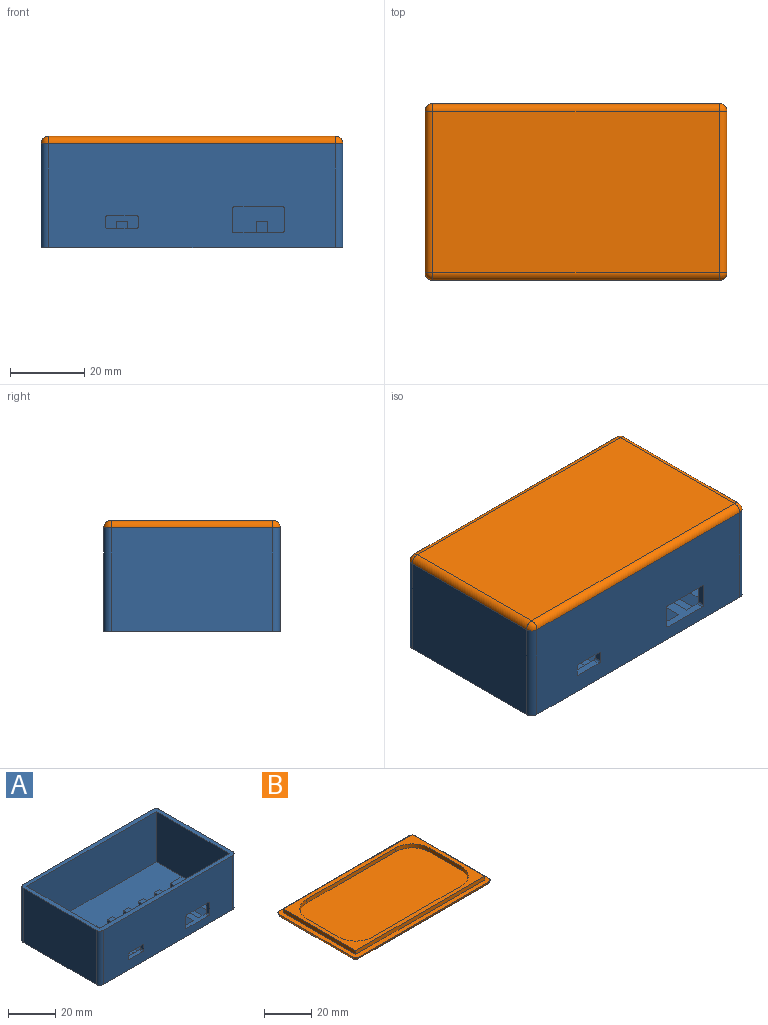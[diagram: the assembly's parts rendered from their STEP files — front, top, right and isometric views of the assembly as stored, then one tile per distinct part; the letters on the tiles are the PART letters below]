
ASSEMBLY  parts=2 mates=1
PART A: 94 faces, bbox 81.4x47.6x28 mm
  f0: plane 77.4x43.6mm, normal (0,0,1), area 1913mm2, adj f1,f2,f3,f14,f15,f16,f58,f61
  f1: plane 77.4x26mm, normal (0,1,0), area 1655.6mm2, adj f0,f5,f14,f16,f17,f18,f19,f20
  f2: plane 6.4x2mm, normal (0,1,0), area 8.8mm2, adj f0,f37,f85,f89
  f3: plane 6.4x2mm, normal (0,1,0), area 8.8mm2, adj f0,f37,f80,f88
  f4: plane 77.4x28mm, normal (0,-1,0), area 2038.1mm2, adj f5,f9,f10,f13,f17,f18,f19,f20
  f5: plane 81.4x47.6mm, normal (0,0,1), area 496.6mm2, adj f1,f4,f6,f7,f8,f10,f11,f12
  f6: plane 43.6x28mm, normal (1,0,0), area 1220.8mm2, adj f5,f9,f10,f11
  f7: plane 77.4x28mm, normal (0,1,0), area 2167.2mm2, adj f5,f9,f11,f12
  f8: plane 43.6x28mm, normal (-1,0,0), area 1220.8mm2, adj f5,f9,f12,f13
  f9: plane 81.4x47.6mm, normal (0,0,-1), area 3871.2mm2, adj f4,f6,f7,f8,f10,f11,f12,f13
  f10: cylinder r=2mm len=28mm, axis (0,0,1), area 88mm2, adj f4,f5,f6,f9
  f11: cylinder r=2mm len=28mm, axis (0,0,-1), area 88mm2, adj f5,f6,f7,f9
  f12: cylinder r=2mm len=28mm, axis (0,0,1), area 88mm2, adj f5,f7,f8,f9
  f13: cylinder r=2mm len=28mm, axis (0,0,-1), area 88mm2, adj f4,f5,f8,f9
  f14: plane 43.6x26mm, normal (-1,0,0), area 1133.6mm2, adj f0,f1,f5,f15,f92
  f15: plane 77.4x26mm, normal (0,-1,0), area 2012.4mm2, adj f0,f5,f14,f16
  f16: plane 43.6x26mm, normal (1,0,0), area 1133.6mm2, adj f0,f1,f5,f15,f93
  f17: plane 7.8x2mm, normal (0,0,1), area 15.6mm2, adj f1,f4,f25,f27
  f18: plane 2.5x2mm, normal (1,0,0), area 5mm2, adj f1,f4,f25,f26
  f19: plane 7.8x2mm, normal (0,0,-1), area 15.6mm2, adj f1,f4,f26,f28
  f20: plane 2.5x2mm, normal (-1,0,0), area 5mm2, adj f1,f4,f27,f28
  f21: plane 6x2mm, normal (-1,0,0), area 12mm2, adj f1,f4,f29,f31
  f22: plane 22.2x13.1mm, normal (0,0,1), area 86.8mm2, adj f1,f4,f29,f30,f72,f86,f87
  f23: plane 6x2mm, normal (1,0,0), area 12mm2, adj f1,f4,f30,f32
  f24: plane 13.1x2mm, normal (0,0,-1), area 26.2mm2, adj f1,f4,f31,f32
  f25: cylinder r=0.5mm len=2mm, axis (0,1,0), area 1.6mm2, adj f1,f4,f17,f18
  f26: cylinder r=0.5mm len=2mm, axis (0,-1,0), area 1.6mm2, adj f1,f4,f18,f19
  f27: cylinder r=0.5mm len=2mm, axis (0,-1,0), area 1.6mm2, adj f1,f4,f17,f20
  f28: cylinder r=0.5mm len=2mm, axis (0,1,0), area 1.6mm2, adj f1,f4,f19,f20
  f29: cylinder r=0.5mm len=2mm, axis (0,1,0), area 1.6mm2, adj f1,f4,f21,f22
  f30: cylinder r=0.5mm len=2mm, axis (0,-1,0), area 1.6mm2, adj f1,f4,f22,f23
  f31: cylinder r=0.5mm len=2mm, axis (0,-1,0), area 1.6mm2, adj f1,f4,f21,f24
  f32: cylinder r=0.5mm len=2mm, axis (0,1,0), area 1.6mm2, adj f1,f4,f23,f24
  f33: plane 18x0.8mm, normal (0,0,-1), area 14.4mm2, adj f1,f34,f40,f41
  f34: cylinder r=1mm len=1mm, axis (0,1,0), area 1.3mm2, adj f1,f33,f35,f41
  f35: plane 2x0.8mm, normal (-1,0,0), area 1.6mm2, adj f1,f34,f36,f41
  f36: cylinder r=1mm len=1mm, axis (0,1,0), area 1.3mm2, adj f1,f35,f37,f41
  f37: plane 21.8x21mm, normal (0,0,1), area 196.2mm2, adj f1,f2,f3,f36,f38,f41,f63,f66
  f38: cylinder r=1mm len=1mm, axis (0,1,0), area 1.3mm2, adj f1,f37,f39,f41
  f39: plane 2x0.8mm, normal (1,0,0), area 1.6mm2, adj f1,f38,f40,f41
  f40: cylinder r=1mm len=1mm, axis (0,1,0), area 1.3mm2, adj f1,f33,f39,f41
  f41: plane 20x4mm, normal (0,1,0), area 79.1mm2, adj f33,f34,f35,f36,f37,f38,f39,f40
  f42: plane 3x3mm, normal (-1,0,0), area 9mm2, adj f66,f67,f68,f89
  f43: plane 3x3mm, normal (1,0,0), area 9mm2, adj f66,f67,f68,f88
  f44: plane 3x3mm, normal (1,0,0), area 9mm2, adj f69,f70,f71,f82
  f45: plane 3x3mm, normal (-1,0,0), area 9mm2, adj f69,f70,f71,f80
  f46: plane 3x3mm, normal (1,0,0), area 9mm2, adj f72,f73,f74,f86
  f47: plane 3x3mm, normal (-1,0,0), area 9mm2, adj f72,f73,f74,f87
  f48: plane 20.2x3mm, normal (0,0,1), area 60.6mm2, adj f1,f75,f81,f91
  f49: plane 3x3mm, normal (-1,0,0), area 9mm2, adj f75,f76,f77,f81
  f50: plane 3x3mm, normal (1,0,0), area 9mm2, adj f63,f64,f65,f85
  f51: plane 3x3mm, normal (-1,0,0), area 9mm2, adj f63,f64,f65,f79
  f52: plane 20.2x3mm, normal (0,0,1), area 60.6mm2, adj f1,f60,f78,f84
  f53: plane 3x3mm, normal (1,0,0), area 9mm2, adj f60,f61,f62,f84
  f54: plane 3x3mm, normal (-1,0,0), area 9mm2, adj f60,f61,f62,f78
  f55: plane 20.2x3mm, normal (0,0,1), area 60.6mm2, adj f1,f57,f83,f90
  f56: plane 3x3mm, normal (1,0,0), area 9mm2, adj f57,f58,f59,f83
  f57: plane 3x3mm, normal (0,-1,0), area 9mm2, adj f55,f56,f59,f90
  f58: plane 14x5mm, normal (0,1,0), area 49.5mm2, adj f0,f56,f59,f83,f93
  f59: plane 23.2x7mm, normal (0,0,1), area 101.8mm2, adj f1,f56,f57,f58,f90,f93
  f60: plane 3x3mm, normal (0,-1,0), area 9mm2, adj f52,f53,f54,f62
  f61: plane 7x5mm, normal (0,1,0), area 19mm2, adj f0,f53,f54,f62,f78,f84
  f62: plane 3x3mm, normal (0,0,1), area 9mm2, adj f53,f54,f60,f61
  f63: plane 3x3mm, normal (0,-1,0), area 9mm2, adj f37,f50,f51,f65
  f64: plane 7x5mm, normal (0,1,0), area 19mm2, adj f0,f50,f51,f65,f79,f85
  f65: plane 3x3mm, normal (0,0,1), area 9mm2, adj f50,f51,f63,f64
  f66: plane 3x3mm, normal (0,-1,0), area 9mm2, adj f37,f42,f43,f68
  f67: plane 7x5mm, normal (0,1,0), area 19mm2, adj f0,f42,f43,f68,f88,f89
  f68: plane 3x3mm, normal (0,0,1), area 9mm2, adj f42,f43,f66,f67
  f69: plane 3x3mm, normal (0,-1,0), area 9mm2, adj f37,f44,f45,f71
  f70: plane 7x5mm, normal (0,1,0), area 19mm2, adj f0,f44,f45,f71,f80,f82
  f71: plane 3x3mm, normal (0,0,1), area 9mm2, adj f44,f45,f69,f70
  f72: plane 3x3mm, normal (0,-1,0), area 9mm2, adj f22,f46,f47,f74
  f73: plane 7x5mm, normal (0,1,0), area 19mm2, adj f0,f46,f47,f74,f86,f87
  f74: plane 3x3mm, normal (0,0,1), area 9mm2, adj f46,f47,f72,f73
  f75: plane 3x3mm, normal (0,-1,0), area 9mm2, adj f48,f49,f77,f91
  f76: plane 14x5mm, normal (0,1,0), area 49.5mm2, adj f0,f49,f77,f81,f92
  f77: plane 23.2x7mm, normal (0,0,1), area 101.8mm2, adj f1,f49,f75,f76,f91,f92
  f78: plane 23.2x2mm, normal (-0.71,0,0.71), area 65.6mm2, adj f0,f1,f52,f54,f61
  f79: plane 23.2x2mm, normal (-0.71,0,0.71), area 65.6mm2, adj f0,f1,f37,f51,f64
  f80: plane 23.2x2mm, normal (-0.71,0,0.71), area 65.6mm2, adj f0,f3,f37,f45,f70
  f81: plane 23.2x2mm, normal (-0.71,0,0.71), area 65.6mm2, adj f0,f1,f48,f49,f76
  f82: plane 23.2x2mm, normal (0.71,0,0.71), area 65.6mm2, adj f0,f1,f37,f44,f70
  f83: plane 23.2x2mm, normal (0.71,0,0.71), area 65.6mm2, adj f0,f1,f55,f56,f58
  f84: plane 23.2x2mm, normal (0.71,0,0.71), area 65.6mm2, adj f0,f1,f52,f53,f61
  f85: plane 23.2x2mm, normal (0.71,0,0.71), area 65.6mm2, adj f0,f2,f37,f50,f64
  f86: plane 23.2x2mm, normal (0.71,0,0.71), area 65.6mm2, adj f0,f1,f22,f46,f73
  f87: plane 23.2x2mm, normal (-0.71,0,0.71), area 65.6mm2, adj f0,f1,f22,f47,f73
  f88: plane 23.2x2mm, normal (0.71,0,0.71), area 65.6mm2, adj f0,f3,f37,f43,f67
  f89: plane 23.2x2mm, normal (-0.71,0,0.71), area 65.6mm2, adj f0,f2,f37,f42,f67
  f90: plane 20.2x3mm, normal (1,0,0), area 60.6mm2, adj f1,f55,f57,f59
  f91: plane 20.2x3mm, normal (-1,0,0), area 60.6mm2, adj f1,f48,f75,f77
  f92: plane 23.2x5mm, normal (0.71,0,0.71), area 164mm2, adj f1,f14,f76,f77
  f93: plane 23.2x5mm, normal (-0.71,0,0.71), area 164mm2, adj f1,f16,f58,f59
PART B: 24 faces, bbox 81.4x47.6x4 mm
  f0: plane 81.4x47.6mm, normal (0,0,1), area 544.8mm2, adj f2,f3,f4,f5,f6,f7,f8,f9
  f1: plane 77.4x43.6mm, normal (0,0,-1), area 3374.6mm2, adj f3,f4,f7,f8
  f2: sphere r=2mm, area 6.3mm2, adj f0,f3,f4
  f3: cylinder r=2mm len=77.4mm, axis (-1,0,0), area 243.2mm2, adj f0,f1,f2,f5
  f4: cylinder r=2mm len=43.6mm, axis (0,-1,0), area 137mm2, adj f0,f1,f2,f6
  f5: sphere r=2mm, area 6.3mm2, adj f0,f3,f7
  f6: sphere r=2mm, area 6.3mm2, adj f0,f4,f8
  f7: cylinder r=2mm len=43.6mm, axis (0,1,0), area 137mm2, adj f0,f1,f5,f9
  f8: cylinder r=2mm len=77.4mm, axis (1,0,0), area 243.2mm2, adj f0,f1,f6,f9
  f9: sphere r=2mm, area 6.3mm2, adj f0,f7,f8
  f10: plane 77x2mm, normal (0,-1,0), area 154mm2, adj f0,f11,f13,f14
  f11: plane 43.2x2mm, normal (1,0,0), area 86.4mm2, adj f0,f10,f12,f14
  f12: plane 77x2mm, normal (0,1,0), area 154mm2, adj f0,f11,f13,f14
  f13: plane 43.2x2mm, normal (-1,0,0), area 86.4mm2, adj f0,f10,f12,f14
  f14: plane 77x43.2mm, normal (0,0,1), area 550.6mm2, adj f10,f11,f12,f13,f16,f17,f18,f19
  f15: plane 73x39.2mm, normal (0,0,1), area 2775.8mm2, adj f16,f17,f18,f19,f20,f21,f22,f23
  f16: plane 53x2mm, normal (0,1,0), area 106mm2, adj f14,f15,f20,f22
  f17: plane 19.2x2mm, normal (-1,0,0), area 38.4mm2, adj f14,f15,f20,f21
  f18: plane 53x2mm, normal (0,-1,0), area 106mm2, adj f14,f15,f21,f23
  f19: plane 19.2x2mm, normal (1,0,0), area 38.4mm2, adj f14,f15,f22,f23
  f20: cylinder r=10mm len=10mm, axis (0,0,-1), area 31.4mm2, adj f14,f15,f16,f17
  f21: cylinder r=10mm len=10mm, axis (0,0,-1), area 31.4mm2, adj f14,f15,f17,f18
  f22: cylinder r=10mm len=10mm, axis (0,0,-1), area 31.4mm2, adj f14,f15,f16,f19
  f23: cylinder r=10mm len=10mm, axis (0,0,-1), area 31.4mm2, adj f14,f15,f18,f19
PLACE A at identity
PLACE B rot(axis=(0,1,0),180deg) t=(0,0,30)mm
MATE fastened A.f5 <-> B.f0  axis (0,0,1) through (38.7,23.8,28)mm
